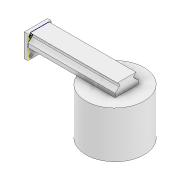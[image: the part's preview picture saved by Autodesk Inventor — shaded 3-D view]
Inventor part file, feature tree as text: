
AUTODESK INVENTOR PART (.ipt)
format: ipt  version: 2021.1 (Build 251245010, 245A)  size: 177,664 bytes
history: native  units: mm
features: sketch x6, extrude x5, plane x4, mirror x2
ambient origin geometry x8: Origin, YZ Plane, XZ Plane, XY Plane, X Axis, Y Axis, Z Axis, Center Point
bodies: Solid1 (feature_tree)
feature tree (17):
  extrude  "Extrusion1"  Depth=40.0mm
  extrude  "Extrusion2"  Depth=6.0mm
  mirror  "Mirror1"
  mirror  "Mirror2"
  plane  "Work Plane4"
  sketch  "Sketch3"  dims[d5=5.0mm d6=6.0mm]
  extrude  "Extrusion3"  Depth=6.0mm
  extrude  "Extrusion4"  [1 undecoded]
  extrude  "Extrusion5"  Depth=7.5mm
  sketch  "Sketch1"  dims[d0=40.0mm d1=40.0mm]
  sketch  "Sketch2"  dims[d2=6.0mm d3=0.0mm d4=5.0mm]
  plane  "Work Plane1"
  plane  "Work Plane2"
  plane  "Work Plane3"
  sketch  "Sketch4"  dims[d7=6.0mm d8=0.0mm d9=-20.0mm]
  sketch  "Sketch5"  dims[d10=15.0mm d12=7.5mm]
  sketch  "Sketch6"  dims[d13=150.0mm d14=0.0mm d15=10.0mm d16=60.0mm d17=40.0mm d20=0.0mm d21=93.0mm d22=70.0mm d23=0.0mm]
note: 1 required parameter value undecoded (feature->parameter linkage not recoverable at this tier; creation-order binding heuristic only, values carry confidence <= 0.55)
